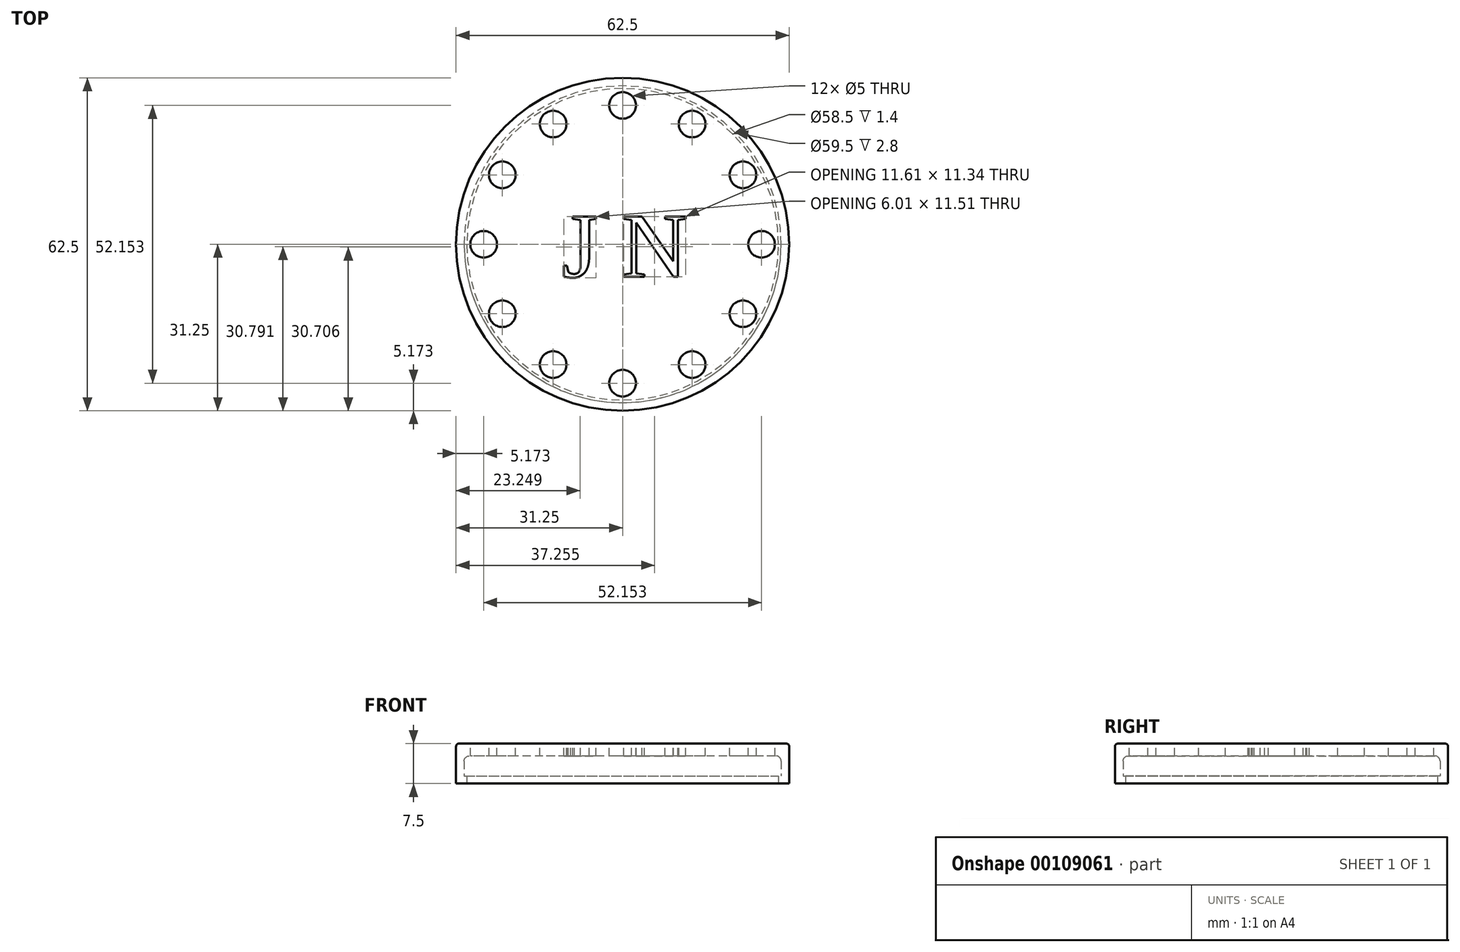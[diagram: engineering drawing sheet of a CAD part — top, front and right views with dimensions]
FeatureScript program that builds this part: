
annotation { "Feature Type Name" : "Feature", "Feature Type Description" : "" }
export const myFeature = defineFeature(function(context is Context, id is Id, definition is map)
    precondition{}
    {
        {
            var Q0;
            Q0=qCreatedBy(makeId("Front.planeOp"),FACE);
            var sketch = newSketch(context, id + "F0", { "sketchPlane" : qUnion([Q0])});
            skLineSegment(sketch, "E0", {"start": v(0, 10.8) * mm, "end": v(-31.25, 10.8) * mm});
            skLineSegment(sketch, "E1", {"start": v(-31.25, 10.8) * mm, "end": v(-31.25, 3.3) * mm});
            skLineSegment(sketch, "E2", {"start": v(-31.25, 3.3) * mm, "end": v(-29.25, 3.3) * mm});
            skLineSegment(sketch, "E3", {"start": v(-29.25, 3.3) * mm, "end": v(-29.25, 4.7) * mm});
            skLineSegment(sketch, "E4", {"start": v(-29.25, 4.7) * mm, "end": v(-29.75, 4.7) * mm});
            skLineSegment(sketch, "E5", {"start": v(-29.75, 4.7) * mm, "end": v(-29.75, 8.5) * mm});
            skLineSegment(sketch, "E6", {"start": v(-29.75, 8.5) * mm, "end": v(0, 8.5) * mm});
            skLineSegment(sketch, "E7", {"start": v(0, 8.5) * mm, "end": v(0, 10.8) * mm});
            skSolve(sketch);
        }
        {
            var Q0;
            Q0=makeQuery(id+"F0.imprint","IMPRINT",FACE,{"disambiguationData":[TD([[makeQuery(id+"F0.imprint","IMPRINT",EDGE,{"derivedFrom":sQuery(id+"F0.wireOp",EDGE,"E0")}),1.0]])]});
            var Q1;
            Q1=sQuery(id+"F0.wireOp",EDGE,"E7");
            revolve(context, id + "F1", {"surfaceOperationType" : NewSurfaceOperationType.NEW, "entities" : qUnion([Q0]), "axis" : qUnion([Q1]), "revolveType" : RevolveType.FULL});
        }
        {
            var Q0;
            Q0=makeQuery(id+"F1.opRevolve","SWEPT_EDGE",EDGE,{"disambiguationData":[OSD([sQuery(id+"F0.wireOp",EDGE,"E5"),sQuery(id+"F0.wireOp",EDGE,"E6")])]});
            fillet(context, id + "F2", {"entities" : qUnion([Q0]), "radius" : 1 * mm, "tangentPropagation" : true, "allowEdgeOverflow" : false});
        }
        {
            var Q0;
            Q0=makeQuery(id+"F1.opRevolve","SWEPT_EDGE",EDGE,{"disambiguationData":[OSD([sQuery(id+"F0.wireOp",EDGE,"E0"),sQuery(id+"F0.wireOp",EDGE,"E1")])]});
            fillet(context, id + "F3", {"entities" : qUnion([Q0]), "radius" : 0.5 * mm, "tangentPropagation" : true, "allowEdgeOverflow" : false});
        }
        {
            var Q0;
            Q0=makeQuery(id+"F1.opRevolve","SWEPT_FACE",FACE,{"disambiguationData":[OSD([sQuery(id+"F0.wireOp",EDGE,"E0")])]});
            var sketch = newSketch(context, id + "F4", { "sketchPlane" : qUnion([Q0])});
            skCircle(sketch, "E8", {"center": v(-26.08, 0) * mm, "radius": 2.5 * mm});
            skCircle(sketch, "E9.1.0", {"center": v(-22.58, -13.04) * mm, "radius": 2.5 * mm});
            skCircle(sketch, "E9.2.0", {"center": v(-13.04, -22.58) * mm, "radius": 2.5 * mm});
            skPoint(sketch, "E9.center", {"position": v(0, 0) * mm});
            skLineSegment(sketch, "E9.anchor1", {"start": v(0, 0) * mm, "end": v(-26.08, 0) * mm, "construction": true});
            skLineSegment(sketch, "E9.anchor2", {"start": v(0, 0) * mm, "end": v(-22.58, 13.04) * mm, "construction": true});
            skCircle(sketch, "E10.1.3.0", {"center": v(0, -26.08) * mm, "radius": 2.5 * mm});
            skCircle(sketch, "E10.1.4.0", {"center": v(13.04, -22.58) * mm, "radius": 2.5 * mm});
            skCircle(sketch, "E10.1.5.0", {"center": v(22.58, -13.04) * mm, "radius": 2.5 * mm});
            skCircle(sketch, "E10.1.6.0", {"center": v(26.08, 0) * mm, "radius": 2.5 * mm});
            skCircle(sketch, "E10.1.7.0", {"center": v(22.58, 13.04) * mm, "radius": 2.5 * mm});
            skCircle(sketch, "E10.1.8.0", {"center": v(13.04, 22.58) * mm, "radius": 2.5 * mm});
            skCircle(sketch, "E10.1.9.0", {"center": v(0, 26.08) * mm, "radius": 2.5 * mm});
            skCircle(sketch, "E11.1.10.0", {"center": v(-13.04, 22.58) * mm, "radius": 2.5 * mm});
            skCircle(sketch, "E11.1.11.0", {"center": v(-22.58, 13.04) * mm, "radius": 2.5 * mm});
            skSolve(sketch);
        }
        {
            var Q0;
            Q0=makeQuery(id+"F4.imprint","IMPRINT",FACE,{"disambiguationData":[TD([[makeQuery(id+"F4.imprint","IMPRINT",EDGE,{"derivedFrom":sQuery(id+"F4.wireOp",EDGE,"E11.1.11.0")}),1.0]])]});
            var Q1;
            Q1=makeQuery(id+"F4.imprint","IMPRINT",FACE,{"disambiguationData":[TD([[makeQuery(id+"F4.imprint","IMPRINT",EDGE,{"derivedFrom":sQuery(id+"F4.wireOp",EDGE,"E8")}),1.0]])]});
            var Q2;
            Q2=makeQuery(id+"F4.imprint","IMPRINT",FACE,{"disambiguationData":[TD([[makeQuery(id+"F4.imprint","IMPRINT",EDGE,{"derivedFrom":sQuery(id+"F4.wireOp",EDGE,"E9.1.0")}),1.0]])]});
            var Q3;
            Q3=makeQuery(id+"F4.imprint","IMPRINT",FACE,{"disambiguationData":[TD([[makeQuery(id+"F4.imprint","IMPRINT",EDGE,{"derivedFrom":sQuery(id+"F4.wireOp",EDGE,"E9.2.0")}),1.0]])]});
            var Q4;
            Q4=makeQuery(id+"F4.imprint","IMPRINT",FACE,{"disambiguationData":[TD([[makeQuery(id+"F4.imprint","IMPRINT",EDGE,{"derivedFrom":sQuery(id+"F4.wireOp",EDGE,"E10.1.3.0")}),1.0]])]});
            var Q5;
            Q5=makeQuery(id+"F4.imprint","IMPRINT",FACE,{"disambiguationData":[TD([[makeQuery(id+"F4.imprint","IMPRINT",EDGE,{"derivedFrom":sQuery(id+"F4.wireOp",EDGE,"E10.1.4.0")}),1.0]])]});
            var Q6;
            Q6=makeQuery(id+"F4.imprint","IMPRINT",FACE,{"disambiguationData":[TD([[makeQuery(id+"F4.imprint","IMPRINT",EDGE,{"derivedFrom":sQuery(id+"F4.wireOp",EDGE,"E10.1.5.0")}),1.0]])]});
            var Q7;
            Q7=makeQuery(id+"F4.imprint","IMPRINT",FACE,{"disambiguationData":[TD([[makeQuery(id+"F4.imprint","IMPRINT",EDGE,{"derivedFrom":sQuery(id+"F4.wireOp",EDGE,"E10.1.6.0")}),1.0]])]});
            var Q8;
            Q8=makeQuery(id+"F4.imprint","IMPRINT",FACE,{"disambiguationData":[TD([[makeQuery(id+"F4.imprint","IMPRINT",EDGE,{"derivedFrom":sQuery(id+"F4.wireOp",EDGE,"E10.1.7.0")}),1.0]])]});
            var Q9;
            Q9=makeQuery(id+"F4.imprint","IMPRINT",FACE,{"disambiguationData":[TD([[makeQuery(id+"F4.imprint","IMPRINT",EDGE,{"derivedFrom":sQuery(id+"F4.wireOp",EDGE,"E10.1.8.0")}),1.0]])]});
            var Q10;
            Q10=makeQuery(id+"F4.imprint","IMPRINT",FACE,{"disambiguationData":[TD([[makeQuery(id+"F4.imprint","IMPRINT",EDGE,{"derivedFrom":sQuery(id+"F4.wireOp",EDGE,"E10.1.9.0")}),1.0]])]});
            var Q11;
            Q11=makeQuery(id+"F4.imprint","IMPRINT",FACE,{"disambiguationData":[TD([[makeQuery(id+"F4.imprint","IMPRINT",EDGE,{"derivedFrom":sQuery(id+"F4.wireOp",EDGE,"E11.1.10.0")}),1.0]])]});
            extrude(context, id + "F5", {"entities" : qUnion([Q0, Q1, Q2, Q3, Q4, Q5, Q6, Q7, Q8, Q9, Q10, Q11]), "operationType" : NewBodyOperationType.REMOVE, "endBound" : BoundingType.THROUGH_ALL, "oppositeDirection" : true, "depth" : 25 * mm});
        }
        {
            var Q0;
            Q0=makeQuery(id+"F1.opRevolve","SWEPT_FACE",FACE,{"disambiguationData":[OSD([sQuery(id+"F0.wireOp",EDGE,"E0")])]});
            var sketch = newSketch(context, id + "F6", { "sketchPlane" : qUnion([Q0])});
            skText(sketch, "E12", { "text": "J N", "fontName": "Tinos-Regular.ttf"});
            const initialGuessF6  = {"E12": [-0.01137, -0.00613, 1, 0, 0.01247]};
            skSetInitialGuess(sketch, initialGuessF6);
            skSolve(sketch);
        }
        {
            var Q0;
            Q0 = qSketchRegion(id + "F6", true);
            extrude(context, id + "F7", {"entities" : qUnion([Q0]), "operationType" : NewBodyOperationType.REMOVE, "endBound" : BoundingType.THROUGH_ALL, "oppositeDirection" : true, "depth" : 25 * mm});
        }
    });
